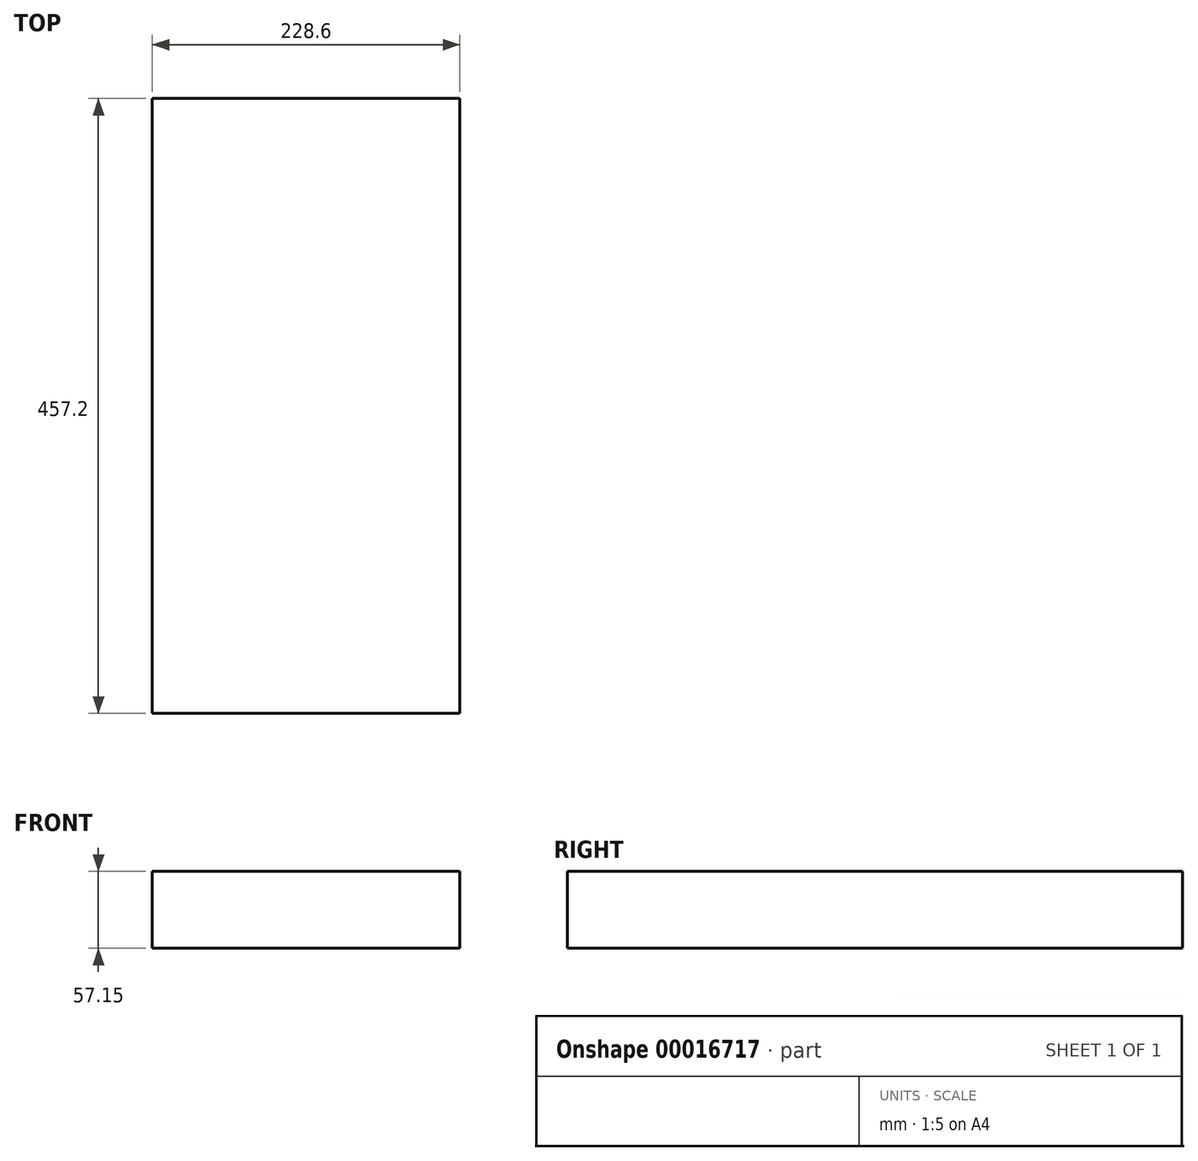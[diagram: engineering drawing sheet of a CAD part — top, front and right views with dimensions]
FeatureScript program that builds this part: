
annotation { "Feature Type Name" : "Feature", "Feature Type Description" : "" }
export const myFeature = defineFeature(function(context is Context, id is Id, definition is map)
    precondition{}
    {
        {
            var Q0;
            Q0=qCreatedBy(makeId("Top.planeOp"),FACE);
            var sketch = newSketch(context, id + "F0", { "sketchPlane" : qUnion([Q0])});
            skLineSegment(sketch, "E0.rect.bottom", {"start": v(114.3, -228.6) * mm, "end": v(-114.3, -228.6) * mm});
            skLineSegment(sketch, "E0.rect.top", {"start": v(114.3, 228.6) * mm, "end": v(-114.3, 228.6) * mm});
            skLineSegment(sketch, "E0.rect.left", {"start": v(114.3, -228.6) * mm, "end": v(114.3, 228.6) * mm});
            skLineSegment(sketch, "E0.rect.right", {"start": v(-114.3, -228.6) * mm, "end": v(-114.3, 228.6) * mm});
            skPoint(sketch, "E0.rect.middle", {"position": v(0, 0) * mm});
            skLineSegment(sketch, "E1", {"start": v(114.3, -160.02) * mm, "end": v(-114.3, -160.02) * mm, "construction": true});
            skLineSegment(sketch, "E2", {"start": v(114.3, -81) * mm, "end": v(-114.3, -81) * mm, "construction": true});
            skSolve(sketch);
        }
        {
            var Q0;
            Q0 = qSketchRegion(id + "F0", true);
            extrude(context, id + "F1", {"entities" : qUnion([Q0]), "oppositeDirection" : true, "depth" : 57.15 * mm});
        }
    });
